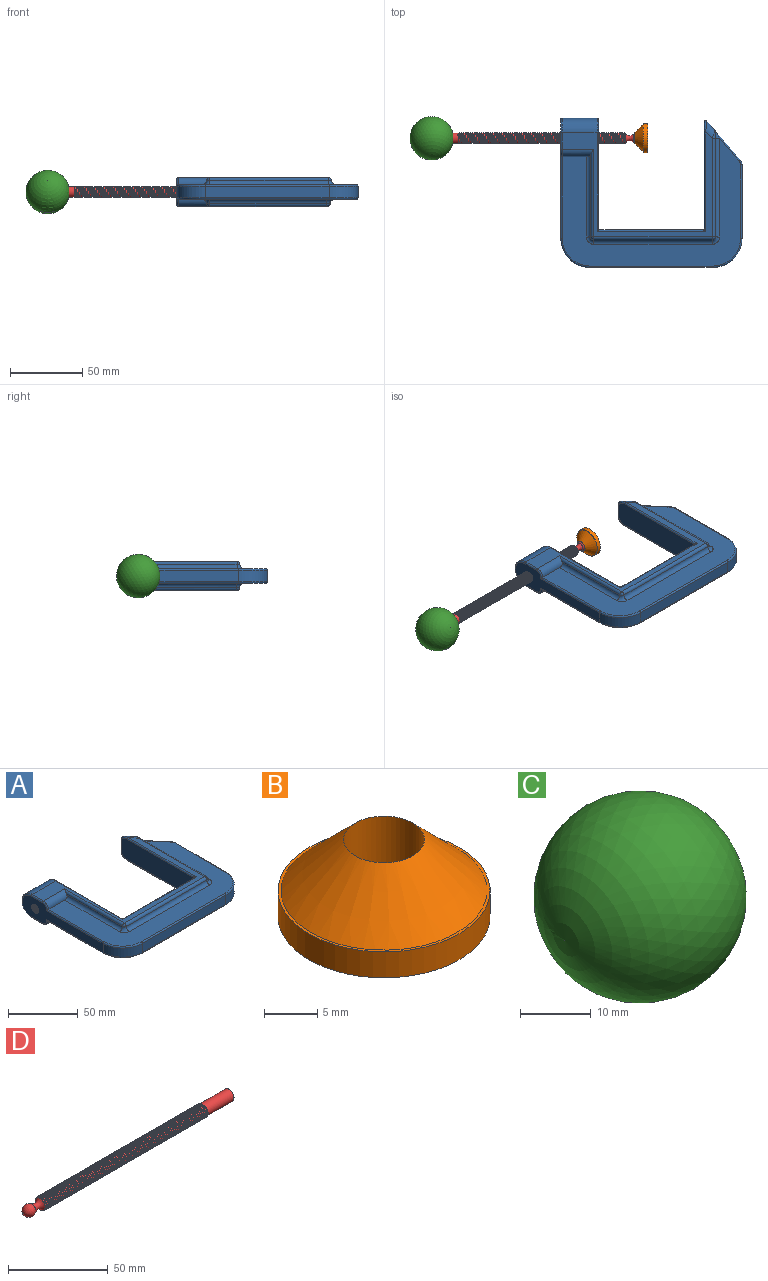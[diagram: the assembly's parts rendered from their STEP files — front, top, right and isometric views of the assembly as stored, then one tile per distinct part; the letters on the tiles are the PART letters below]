
ASSEMBLY  parts=4 mates=3
PART A: 90 faces, bbox 128.8x106x22.2 mm
  f0: cylinder r=3mm len=20.27mm, axis (1,0,0), area 38.4mm2, adj f58,f59,f60,f88
  f1: plane 123x88.12mm, normal (0,0,1), area 3643.4mm2, adj f19,f51,f52,f53,f54,f55,f56,f57
  f2: plane 123x89.02mm, normal (0,0,-1), area 3736.9mm2, adj f18,f39,f40,f41,f42,f43,f44,f45
  f3: plane 82.14x18.14mm, normal (-1,0,0), area 819.2mm2, adj f13,f45,f46,f47,f48,f49,f50,f51
  f4: plane 85x8mm, normal (0,-1,0), area 680mm2, adj f12,f13,f43,f53
  f5: plane 50.77x8mm, normal (1,0,0), area 406.2mm2, adj f12,f14,f41,f55
  f6: plane 26.92x23.04mm, normal (0.76,0.65,0), area 283.5mm2, adj f14,f34,f39,f57
  f7: plane 73.29x18mm, normal (-1,0,0), area 1308.7mm2, adj f30,f32,f34,f36,f38,f68
  f8: plane 71x18mm, normal (0,1,0), area 1278mm2, adj f29,f37,f65,f68
  f9: plane 75x18mm, normal (1,0,0), area 1212.5mm2, adj f31,f33,f35,f65,f89
  f10: plane 102.79x72.95mm, normal (0,0,-1), area 953.1mm2, adj f16,f17,f18,f20,f22,f23,f35,f37
  f11: plane 103.57x73.13mm, normal (0,0,1), area 1038.1mm2, adj f15,f17,f19,f25,f26,f27,f29,f30
  f12: cylinder r=20mm len=20mm, axis (0,0,-1), area 251.3mm2, adj f4,f5,f42,f54
  f13: cylinder r=20mm len=20mm, axis (0,0,1), area 251.3mm2, adj f3,f4,f44,f52
  f14: cylinder r=5mm len=8mm, axis (0,0,-1), area 28.3mm2, adj f5,f6,f40,f56
  f15: cylinder r=5mm len=12.13mm, axis (0.65,-0.76,0), area 62.5mm2, adj f11,f28,f32,f86
  f16: cylinder r=5mm len=11.22mm, axis (0.65,-0.76,0), area 52.9mm2, adj f10,f21,f36,f77
  f17: cylinder r=10mm len=24mm, axis (1,0,0), area 754mm2, adj f10,f11,f33,f48
  f18: cylinder r=5mm len=21.66mm, axis (1,0,0), area 154.2mm2, adj f2,f10,f20,f46,f70
  f19: cylinder r=5mm len=21.66mm, axis (-1,0,0), area 154.2mm2, adj f1,f11,f25,f50,f79
  f20: cylinder r=2mm len=60.33mm, axis (0,-1,0), area 183.2mm2, adj f10,f18,f24,f70
  f21: bspline ~5.89x5.37mm, area 14.6mm2, adj f16,f22,f75,f76
  f22: cylinder r=2mm len=68.54mm, axis (0.01,1,0), area 215.3mm2, adj f10,f21,f63,f74
  f23: cylinder r=2mm len=80.62mm, axis (1,0,0), area 253.3mm2, adj f10,f24,f63,f72
  f24: sphere r=2mm, area 6.3mm2, adj f20,f23,f71
  f25: cylinder r=2mm len=60.51mm, axis (0,1,0), area 183.8mm2, adj f11,f19,f61,f79
  f26: cylinder r=2mm len=81.91mm, axis (-1,0,0), area 257.3mm2, adj f11,f61,f62,f81
  f27: cylinder r=2mm len=67.79mm, axis (0,-1,0), area 213mm2, adj f11,f28,f62,f83
  f28: bspline ~6.97x6.08mm, area 14.7mm2, adj f15,f27,f84,f85
  f29: cylinder r=1mm len=75mm, axis (1,0,0), area 114.7mm2, adj f8,f11,f66,f69
  f30: cylinder r=1mm len=69.14mm, axis (0,1,0), area 107mm2, adj f7,f11,f32,f69
  f31: cylinder r=1mm len=68mm, axis (0,-1,0), area 105.2mm2, adj f9,f11,f33,f66
  f32: bspline ~10.04x6.48mm, area 19.1mm2, adj f7,f15,f30,f34,f87
  f33: torus R=9mm, axis (1,0,0), area 47.6mm2, adj f9,f17,f31,f35
  f34: cylinder r=1mm len=10mm, axis (0,0,1), area 23.9mm2, adj f6,f7,f32,f36,f39,f57,f78,f87
  f35: cylinder r=1mm len=68mm, axis (0,-1,0), area 105.2mm2, adj f9,f10,f33,f64
  f36: bspline ~10.04x6.48mm, area 19.1mm2, adj f7,f16,f34,f38,f78
  f37: cylinder r=1mm len=75mm, axis (1,0,0), area 114.7mm2, adj f8,f10,f64,f67
  f38: cylinder r=1mm len=69.14mm, axis (0,1,0), area 107mm2, adj f7,f10,f36,f67
  f39: cylinder r=1mm len=27.65mm, axis (-0.65,0.76,0), area 40.4mm2, adj f2,f6,f34,f40,f76,f77,f78
  f40: torus R=4mm, axis (0,0,1), area 5.2mm2, adj f2,f14,f39,f41
  f41: cylinder r=1mm len=50.77mm, axis (0,1,0), area 79.8mm2, adj f2,f5,f40,f42
  f42: torus R=19mm, axis (0,0,1), area 48.5mm2, adj f2,f12,f41,f43
  f43: cylinder r=1mm len=85mm, axis (1,0,0), area 133.5mm2, adj f2,f4,f42,f44
  f44: torus R=19mm, axis (0,0,1), area 48.5mm2, adj f2,f13,f43,f45
  f45: cylinder r=1mm len=57.64mm, axis (0,-1,0), area 89.7mm2, adj f2,f3,f44,f46
  f46: torus R=4mm, axis (1,0,0), area 12.3mm2, adj f3,f18,f45,f47
  f47: cylinder r=1mm len=11.48mm, axis (0,1,0), area 18mm2, adj f3,f10,f46,f48
  f48: torus R=9mm, axis (1,0,0), area 47.6mm2, adj f3,f17,f47,f49
  f49: cylinder r=1mm len=11.48mm, axis (0,1,0), area 18mm2, adj f3,f11,f48,f50
  f50: torus R=4mm, axis (1,0,0), area 12.3mm2, adj f3,f19,f49,f51
  f51: cylinder r=1mm len=57.64mm, axis (0,1,0), area 89.7mm2, adj f1,f3,f50,f52
  f52: torus R=19mm, axis (0,0,1), area 48.5mm2, adj f1,f13,f51,f53
  f53: cylinder r=1mm len=85mm, axis (-1,0,0), area 133.5mm2, adj f1,f4,f52,f54
  f54: torus R=19mm, axis (0,0,1), area 48.5mm2, adj f1,f12,f53,f55
  f55: cylinder r=1mm len=50.77mm, axis (0,-1,0), area 79.8mm2, adj f1,f5,f54,f56
  f56: torus R=4mm, axis (0,0,1), area 5.2mm2, adj f1,f14,f55,f57
  f57: cylinder r=1mm len=27.65mm, axis (0.65,-0.76,0), area 38.7mm2, adj f1,f6,f34,f56,f85,f86,f87
  f58: cone r=3.5mm half-angle=45deg, axis (-1,0,0), area 6.3mm2, adj f0,f3,f59,f60
  f59: bspline ~21.96x8.93mm, area 356mm2, adj f0,f3,f58,f60,f88
  f60: bspline ~21.75x8.93mm, area 357mm2, adj f0,f3,f58,f59,f88
  f61: sphere r=2mm, area 6.3mm2, adj f25,f26,f80
  f62: sphere r=2mm, area 6.3mm2, adj f26,f27,f82
  f63: sphere r=2mm, area 6.3mm2, adj f22,f23,f73
  f64: bspline ~2x2mm, area 1.1mm2, adj f35,f37,f65
  f65: cylinder r=1mm len=18mm, axis (0,0,-1), area 28.3mm2, adj f8,f9,f64,f66
  f66: bspline ~2x2mm, area 1.1mm2, adj f29,f31,f65
  f67: bspline ~2x2mm, area 1.1mm2, adj f37,f38,f68
  f68: cylinder r=1mm len=18mm, axis (0,0,1), area 28.3mm2, adj f7,f8,f67,f69
  f69: bspline ~2x2mm, area 1.1mm2, adj f29,f30,f68
  f70: cylinder r=3mm len=56.33mm, axis (0,-1,0), area 263.1mm2, adj f2,f18,f20,f71
  f71: torus R=5mm, axis (0,0,1), area 22.9mm2, adj f2,f24,f70,f72
  f72: cylinder r=3mm len=80.62mm, axis (1,0,0), area 379.9mm2, adj f2,f23,f71,f73
  f73: torus R=5mm, axis (0,0,1), area 22.8mm2, adj f2,f63,f72,f74
  f74: cylinder r=3mm len=68.54mm, axis (0.01,1,0), area 322.9mm2, adj f2,f22,f73,f75
  f75: bspline ~3.01x3mm, area 1.6mm2, adj f2,f21,f74,f76
  f76: bspline ~6.6x3.9mm, area 16.9mm2, adj f21,f39,f75,f77
  f77: cylinder r=3mm len=5.37mm, axis (-0.65,0.76,0), area 3.7mm2, adj f16,f39,f76,f78
  f78: bspline ~1.05x0.98mm, area 0.2mm2, adj f34,f36,f39,f77
  f79: cylinder r=3mm len=56.51mm, axis (0,-1,0), area 263.9mm2, adj f1,f19,f25,f80
  f80: torus R=5mm, axis (0,0,1), area 22.9mm2, adj f1,f61,f79,f81
  f81: cylinder r=3mm len=81.91mm, axis (1,0,0), area 386mm2, adj f1,f26,f80,f82
  f82: torus R=5mm, axis (0,0,1), area 22.9mm2, adj f1,f62,f81,f83
  f83: cylinder r=3mm len=67.79mm, axis (0,1,0), area 319.5mm2, adj f1,f27,f82,f84
  f84: bspline ~3x3mm, area 1.5mm2, adj f1,f28,f83,f85
  f85: bspline ~6.06x3.9mm, area 17.1mm2, adj f28,f57,f84,f86
  f86: cylinder r=3mm len=6.23mm, axis (0.65,-0.76,0), area 4.3mm2, adj f15,f57,f85,f87
  f87: bspline ~1.05x0.97mm, area 0.2mm2, adj f32,f34,f57,f86
  f88: plane 11.99x11.99mm, normal (1,0,0), area 67.3mm2, adj f0,f59,f60,f89
  f89: cylinder r=5.72mm len=11.44mm, axis (1,0,0), area 187.9mm2, adj f9,f88
PART B: 6 faces, bbox 20x20x8.9 mm
  f0: plane 20x20mm, normal (0,0,1), area 17.8mm2, adj f1,f3
  f1: cylinder r=10mm len=20mm, axis (0,0,-1), area 188.5mm2, adj f0,f2
  f2: plane 20x20mm, normal (0,0,-1), area 314.2mm2, adj f1
  f3: cone r=9.81mm half-angle=45deg, axis (0,0,-1), area 354.7mm2, adj f0,f4
  f4: cylinder r=3.81mm len=7.62mm, axis (0,0,1), area 141.3mm2, adj f3,f5
  f5: plane 7.62x7.62mm, normal (0,0,1), area 45.6mm2, adj f4
PART C: 3 faces, bbox 30x30x30 mm
  f0: sphere r=15mm, area 2788.4mm2, adj f1
  f1: cylinder r=3.5mm len=14.59mm, axis (0,0,1), area 320.8mm2, adj f0,f2
  f2: plane 7x7mm, normal (0,0,-1), area 38.5mm2, adj f1
PART D: 107 faces, bbox 145.3x7.9x9.1 mm
  f0: bspline ~15.08x8.93mm, area 110.1mm2, adj f1,f2,f3,f4,f5,f6,f7,f8
  f1: bspline ~15.08x8.93mm, area 111.7mm2, adj f0,f2,f3,f4,f5,f6,f7,f8
  f2: cylinder r=3.5mm len=7mm, axis (-1,0,0), area 18.3mm2, adj f0,f1,f3,f13,f102
  f3: cylinder r=3.5mm len=7mm, axis (-1,0,0), area 18.3mm2, adj f0,f1,f2,f4
  f4: cylinder r=3.5mm len=7mm, axis (-1,0,0), area 18.3mm2, adj f0,f1,f3,f5
  f5: cylinder r=3.5mm len=7mm, axis (-1,0,0), area 18.3mm2, adj f0,f1,f4,f6
  f6: cylinder r=3.5mm len=7mm, axis (-1,0,0), area 18.3mm2, adj f0,f1,f5,f7
  f7: cylinder r=3.5mm len=7mm, axis (-1,0,0), area 18.3mm2, adj f0,f1,f6,f8
  f8: cylinder r=3.5mm len=7mm, axis (-1,0,0), area 18.3mm2, adj f0,f1,f7,f9
  f9: cylinder r=3.5mm len=7mm, axis (-1,0,0), area 18.3mm2, adj f0,f1,f8,f10
  f10: cylinder r=3.5mm len=7mm, axis (-1,0,0), area 18.3mm2, adj f0,f1,f9,f11
  f11: cylinder r=3.5mm len=7mm, axis (-1,0,0), area 18.3mm2, adj f0,f1,f10,f12
  f12: cylinder r=3.5mm len=7mm, axis (-1,0,0), area 24.4mm2, adj f0,f1,f11,f105
  f13: cylinder r=3.5mm len=7mm, axis (-1,0,0), area 18.2mm2, adj f1,f2,f14,f102,f103
  f14: cylinder r=3.5mm len=7mm, axis (-1,0,0), area 18.3mm2, adj f13,f15,f102,f103
  f15: cylinder r=3.5mm len=7mm, axis (-1,0,0), area 18.3mm2, adj f14,f16,f102,f103
  f16: cylinder r=3.5mm len=7mm, axis (-1,0,0), area 18.3mm2, adj f15,f17,f102,f103
  f17: cylinder r=3.5mm len=7mm, axis (-1,0,0), area 18.3mm2, adj f16,f18,f102,f103
  f18: cylinder r=3.5mm len=7mm, axis (-1,0,0), area 18.3mm2, adj f17,f19,f102,f103
  f19: cylinder r=3.5mm len=7mm, axis (-1,0,0), area 18.3mm2, adj f18,f20,f102,f103
  f20: cylinder r=3.5mm len=7mm, axis (-1,0,0), area 18.3mm2, adj f19,f21,f102,f103
  f21: cylinder r=3.5mm len=7mm, axis (-1,0,0), area 18.3mm2, adj f20,f22,f102,f103
  f22: cylinder r=3.5mm len=7mm, axis (-1,0,0), area 18.3mm2, adj f21,f23,f102,f103
  f23: cylinder r=3.5mm len=7mm, axis (-1,0,0), area 18.3mm2, adj f22,f24,f102,f103
  f24: cylinder r=3.5mm len=7mm, axis (-1,0,0), area 18.3mm2, adj f23,f25,f102,f103
  f25: cylinder r=3.5mm len=7mm, axis (-1,0,0), area 18.3mm2, adj f24,f26,f102,f103
  f26: cylinder r=3.5mm len=7mm, axis (-1,0,0), area 18.3mm2, adj f25,f27,f102,f103
  f27: cylinder r=3.5mm len=7mm, axis (-1,0,0), area 18.3mm2, adj f26,f28,f102,f103
  f28: cylinder r=3.5mm len=7mm, axis (-1,0,0), area 18.3mm2, adj f27,f29,f102,f103
  f29: cylinder r=3.5mm len=7mm, axis (-1,0,0), area 18.3mm2, adj f28,f30,f102,f103
  f30: cylinder r=3.5mm len=7mm, axis (-1,0,0), area 18.3mm2, adj f29,f31,f102,f103
  f31: cylinder r=3.5mm len=7mm, axis (-1,0,0), area 18.3mm2, adj f30,f32,f102,f103
  f32: cylinder r=3.5mm len=7mm, axis (-1,0,0), area 18.3mm2, adj f31,f33,f100,f102,f103
  f33: cylinder r=3.5mm len=7mm, axis (-1,0,0), area 18.2mm2, adj f32,f34,f100,f101,f103
  f34: cylinder r=3.5mm len=7mm, axis (-1,0,0), area 18.3mm2, adj f33,f35,f100,f101
  f35: cylinder r=3.5mm len=7mm, axis (-1,0,0), area 18.3mm2, adj f34,f36,f100,f101
  f36: cylinder r=3.5mm len=7mm, axis (-1,0,0), area 18.3mm2, adj f35,f37,f100,f101
  f37: cylinder r=3.5mm len=7mm, axis (-1,0,0), area 18.3mm2, adj f36,f38,f100,f101
  f38: cylinder r=3.5mm len=7mm, axis (-1,0,0), area 18.3mm2, adj f37,f39,f100,f101
  f39: cylinder r=3.5mm len=7mm, axis (-1,0,0), area 18.3mm2, adj f38,f40,f100,f101
  f40: cylinder r=3.5mm len=7mm, axis (-1,0,0), area 18.3mm2, adj f39,f41,f100,f101
  f41: cylinder r=3.5mm len=7mm, axis (-1,0,0), area 18.3mm2, adj f40,f42,f100,f101
  f42: cylinder r=3.5mm len=7mm, axis (-1,0,0), area 18.3mm2, adj f41,f43,f100,f101
  f43: cylinder r=3.5mm len=7mm, axis (-1,0,0), area 18.3mm2, adj f42,f44,f100,f101
  f44: cylinder r=3.5mm len=7mm, axis (-1,0,0), area 18.3mm2, adj f43,f45,f100,f101
  f45: cylinder r=3.5mm len=7mm, axis (-1,0,0), area 18.3mm2, adj f44,f46,f100,f101
  f46: cylinder r=3.5mm len=7mm, axis (-1,0,0), area 18.3mm2, adj f45,f47,f100,f101
  f47: cylinder r=3.5mm len=7mm, axis (-1,0,0), area 18.3mm2, adj f46,f48,f100,f101
  f48: cylinder r=3.5mm len=7mm, axis (-1,0,0), area 18.3mm2, adj f47,f49,f100,f101
  f49: cylinder r=3.5mm len=7mm, axis (-1,0,0), area 18.3mm2, adj f48,f50,f100,f101
  f50: cylinder r=3.5mm len=7mm, axis (-1,0,0), area 18.3mm2, adj f49,f51,f100,f101
  f51: cylinder r=3.5mm len=7mm, axis (-1,0,0), area 18.3mm2, adj f50,f52,f100,f101
  f52: cylinder r=3.5mm len=7mm, axis (-1,0,0), area 18.3mm2, adj f51,f53,f98,f100,f101
  f53: cylinder r=3.5mm len=7mm, axis (-1,0,0), area 18.2mm2, adj f52,f54,f98,f99,f101
  f54: cylinder r=3.5mm len=7mm, axis (-1,0,0), area 18.3mm2, adj f53,f55,f98,f99
  f55: cylinder r=3.5mm len=7mm, axis (-1,0,0), area 18.3mm2, adj f54,f56,f98,f99
  f56: cylinder r=3.5mm len=7mm, axis (-1,0,0), area 18.3mm2, adj f55,f57,f98,f99
  f57: cylinder r=3.5mm len=7mm, axis (-1,0,0), area 18.3mm2, adj f56,f58,f98,f99
  f58: cylinder r=3.5mm len=7mm, axis (-1,0,0), area 18.3mm2, adj f57,f59,f98,f99
  f59: cylinder r=3.5mm len=7mm, axis (-1,0,0), area 18.3mm2, adj f58,f60,f98,f99
  f60: cylinder r=3.5mm len=7mm, axis (-1,0,0), area 18.3mm2, adj f59,f61,f98,f99
  f61: cylinder r=3.5mm len=7mm, axis (-1,0,0), area 18.3mm2, adj f60,f62,f98,f99
  f62: cylinder r=3.5mm len=7mm, axis (-1,0,0), area 18.3mm2, adj f61,f63,f98,f99
  f63: cylinder r=3.5mm len=7mm, axis (-1,0,0), area 18.3mm2, adj f62,f64,f98,f99
  f64: cylinder r=3.5mm len=7mm, axis (-1,0,0), area 18.3mm2, adj f63,f65,f98,f99
  f65: cylinder r=3.5mm len=7mm, axis (-1,0,0), area 18.3mm2, adj f64,f66,f98,f99
  f66: cylinder r=3.5mm len=7mm, axis (-1,0,0), area 18.3mm2, adj f65,f67,f98,f99
  f67: cylinder r=3.5mm len=7mm, axis (-1,0,0), area 18.3mm2, adj f66,f68,f98,f99
  f68: cylinder r=3.5mm len=7mm, axis (-1,0,0), area 18.3mm2, adj f67,f69,f98,f99
  f69: cylinder r=3.5mm len=7mm, axis (-1,0,0), area 18.3mm2, adj f68,f70,f98,f99
  f70: cylinder r=3.5mm len=7mm, axis (-1,0,0), area 18.3mm2, adj f69,f71,f98,f99
  f71: cylinder r=3.5mm len=7mm, axis (-1,0,0), area 18.3mm2, adj f70,f72,f98,f99
  f72: cylinder r=3.5mm len=7mm, axis (-1,0,0), area 18.3mm2, adj f71,f73,f96,f98,f99
  f73: cylinder r=3.5mm len=7mm, axis (-1,0,0), area 18.2mm2, adj f72,f74,f96,f97,f99
  f74: cylinder r=3.5mm len=7mm, axis (-1,0,0), area 18.3mm2, adj f73,f75,f96,f97
  f75: cylinder r=3.5mm len=7mm, axis (-1,0,0), area 18.3mm2, adj f74,f76,f96,f97
  f76: cylinder r=3.5mm len=7mm, axis (-1,0,0), area 18.3mm2, adj f75,f77,f96,f97
  f77: cylinder r=3.5mm len=7mm, axis (-1,0,0), area 18.3mm2, adj f76,f78,f96,f97
  f78: cylinder r=3.5mm len=7mm, axis (-1,0,0), area 18.3mm2, adj f77,f79,f96,f97
  f79: cylinder r=3.5mm len=7mm, axis (-1,0,0), area 18.3mm2, adj f78,f80,f96,f97
  f80: cylinder r=3.5mm len=7mm, axis (-1,0,0), area 18.3mm2, adj f79,f81,f96,f97
  f81: cylinder r=3.5mm len=7mm, axis (-1,0,0), area 18.3mm2, adj f80,f82,f96,f97
  f82: cylinder r=3.5mm len=7mm, axis (-1,0,0), area 18.3mm2, adj f81,f83,f96,f97
  f83: cylinder r=3.5mm len=7mm, axis (-1,0,0), area 18.3mm2, adj f82,f84,f96,f97
  f84: cylinder r=3.5mm len=7mm, axis (-1,0,0), area 18.3mm2, adj f83,f85,f96,f97
  f85: cylinder r=3.5mm len=7mm, axis (-1,0,0), area 18.3mm2, adj f84,f86,f96,f97
  f86: cylinder r=3.5mm len=7mm, axis (-1,0,0), area 18.3mm2, adj f85,f87,f96,f97
  f87: cylinder r=3.5mm len=7mm, axis (-1,0,0), area 18.3mm2, adj f86,f88,f96,f97
  f88: cylinder r=3.5mm len=7mm, axis (-1,0,0), area 18.3mm2, adj f87,f89,f96,f97
  f89: cylinder r=3.5mm len=7mm, axis (-1,0,0), area 18.3mm2, adj f88,f90,f96,f97
  f90: cylinder r=3.5mm len=7mm, axis (-1,0,0), area 18.3mm2, adj f89,f91,f96,f97
  f91: cylinder r=3.5mm len=7mm, axis (-1,0,0), area 18.3mm2, adj f90,f92,f96,f97
  f92: cylinder r=3.5mm len=7mm, axis (-1,0,0), area 18.3mm2, adj f91,f93,f96,f97
  f93: cylinder r=3.5mm len=19.89mm, axis (-1,0,0), area 419.6mm2, adj f92,f94,f95,f96,f97
  f94: plane 7x7mm, normal (1,0,0), area 38.5mm2, adj f93
  f95: plane 0.43x0.35mm, normal (0,0.95,0.31), area 0.1mm2, adj f93,f96,f97
  f96: bspline ~26.54x8.93mm, area 200.9mm2, adj f72,f73,f74,f75,f76,f77,f78,f79
  f97: bspline ~26.54x8.93mm, area 200.3mm2, adj f73,f74,f75,f76,f77,f78,f79,f80
  f98: bspline ~25.71x8.93mm, area 193.3mm2, adj f52,f53,f54,f55,f56,f57,f58,f59
  f99: bspline ~25.5x8.93mm, area 192.1mm2, adj f53,f54,f55,f56,f57,f58,f59,f60
  f100: bspline ~25.71x8.93mm, area 193.3mm2, adj f32,f33,f34,f35,f36,f37,f38,f39
  f101: bspline ~25.5x8.93mm, area 192.1mm2, adj f33,f34,f35,f36,f37,f38,f39,f40
  f102: bspline ~25.71x8.93mm, area 193.3mm2, adj f0,f2,f13,f14,f15,f16,f17,f18
  f103: bspline ~25.5x8.93mm, area 192.1mm2, adj f1,f13,f14,f15,f16,f17,f18,f19
  f104: revolved ~6.87x6.87mm, area 122.8mm2, adj f105
  f105: revolved ~6.98x6.98mm, area 91.1mm2, adj f12,f104,f106
  f106: plane 6.19x2.87mm, normal (-1,0,0), area 1.4mm2, adj f0,f1,f105
PLACE A at identity fixed
PLACE B rot(axis=(0.13,-0.98,-0.13),91deg) t=(-2.56,77.54,0)mm
PLACE C rot(axis=(-0.66,-0.37,0.66),139.8deg) t=(-151.62,77.54,0)mm
PLACE D rot(axis=(0,-0.96,0.27),180deg) t=(-45.32,11.64,40.84)mm
MATE cylindrical D.f2 <-> A.f0  axis (-1,0,0) through (-151.62,77.54,0)mm
MATE fastened C.f1 <-> D.f2  axis (-1,0,0) through (-151.62,77.54,0)mm
MATE ball B.f3 <-> D.f2  axis (1,0,0) through (-11.46,77.54,0)mm
